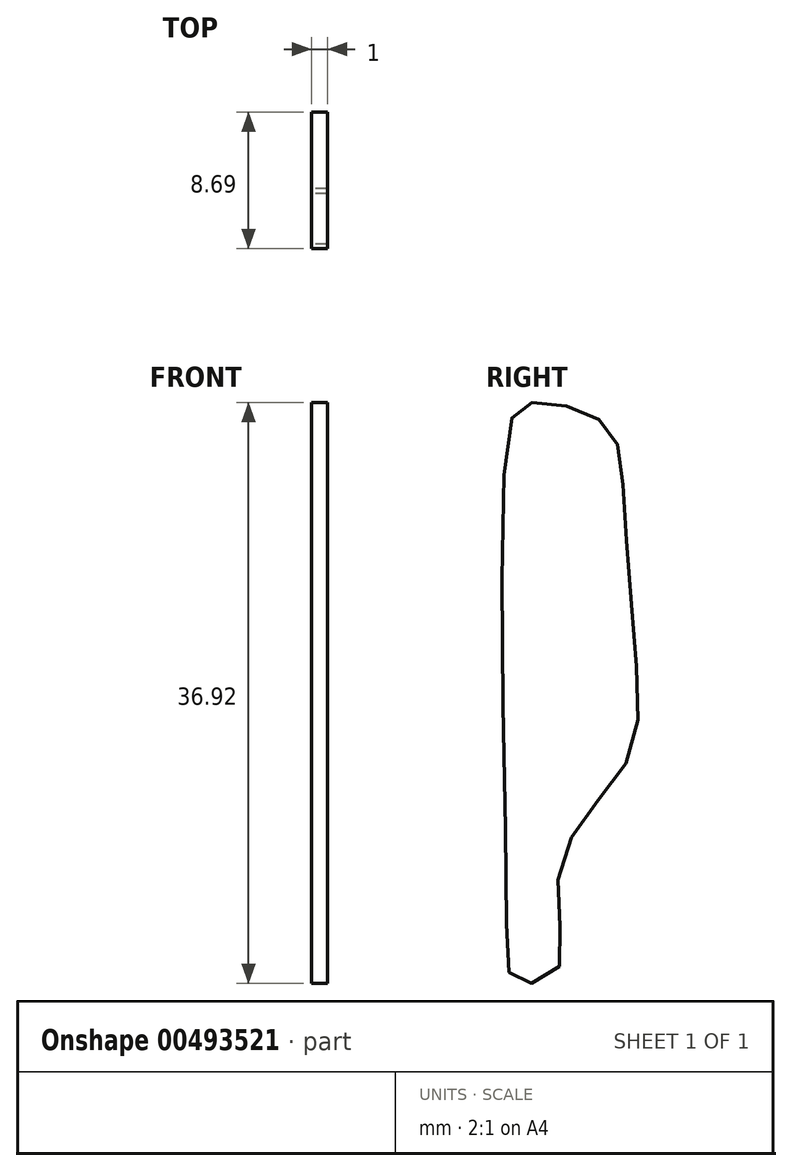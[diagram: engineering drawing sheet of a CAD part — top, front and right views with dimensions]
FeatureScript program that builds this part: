
annotation { "Feature Type Name" : "Feature", "Feature Type Description" : "" }
export const myFeature = defineFeature(function(context is Context, id is Id, definition is map)
    precondition{}
    {
        {
            var Q0;
            Q0=qCreatedBy(makeId("Right.planeOp"),FACE);
            var sketch = newSketch(context, id + "F0", { "sketchPlane" : qUnion([Q0])});
            skFitSpline(sketch, "E0", {"points": [v(-24.4, -13.68) * mm, v(-24.4, 16.88) * mm, v(-23.17, 19.35) * mm, v(-20.21, 19.1) * mm, v(-17.75, 17.62) * mm, v(-17, 13.93) * mm, v(-16.27, 4.07) * mm, v(-16.51, -2.83) * mm, v(-19.72, -7.27) * mm, v(-21.2, -12.2) * mm, v(-21.2, -16.64) * mm, v(-23.66, -17.38) * mm, v(-24.4, -13.68) * mm]});
            skSolve(sketch);
        }
        {
            var Q0;
            Q0 = qSketchRegion(id + "F0", true);
            extrude(context, id + "F1", {"entities" : qUnion([Q0]), "depth" : 1 * mm});
        }
    });
